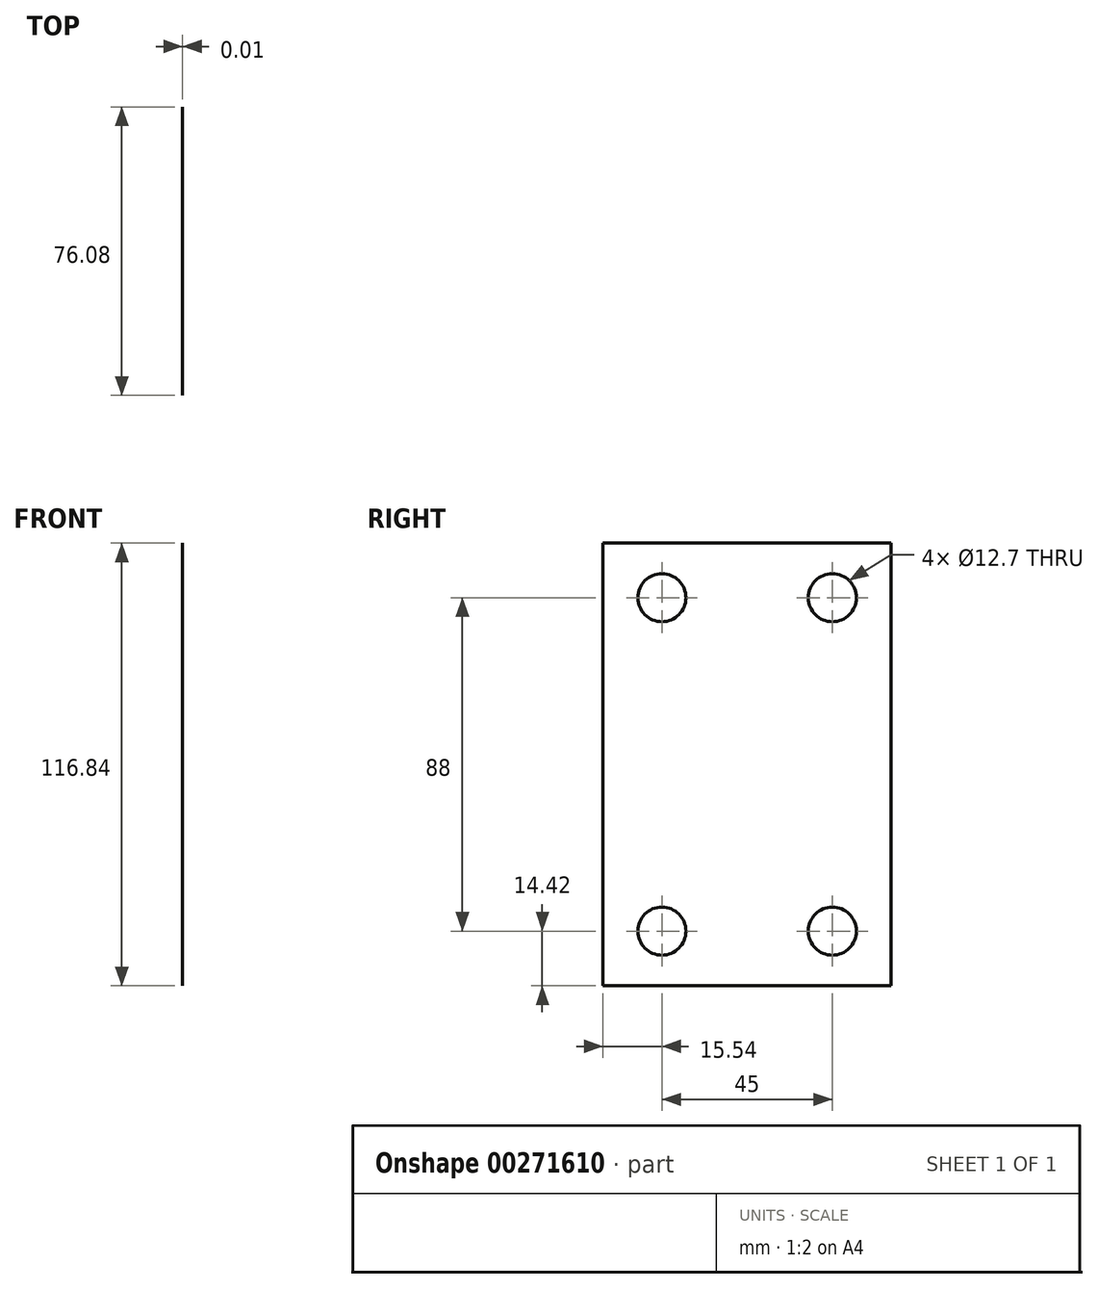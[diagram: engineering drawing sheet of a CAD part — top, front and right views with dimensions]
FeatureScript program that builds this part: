
annotation { "Feature Type Name" : "Feature", "Feature Type Description" : "" }
export const myFeature = defineFeature(function(context is Context, id is Id, definition is map)
    precondition{}
    {
        {
            var Q0;
            Q0=qCreatedBy(makeId("Right.planeOp"),FACE);
            var sketch = newSketch(context, id + "F0", { "sketchPlane" : qUnion([Q0])});
            skLineSegment(sketch, "E0.bottom", {"start": v(38.04, 58.42) * mm, "end": v(-38.04, 58.42) * mm});
            skLineSegment(sketch, "E0.top", {"start": v(38.04, -58.42) * mm, "end": v(-38.04, -58.42) * mm});
            skLineSegment(sketch, "E0.left", {"start": v(38.04, 58.42) * mm, "end": v(38.04, -58.42) * mm});
            skLineSegment(sketch, "E0.right", {"start": v(-38.04, 58.42) * mm, "end": v(-38.04, -58.42) * mm});
            skPoint(sketch, "E0.middle", {"position": v(0, 0) * mm});
            skCircle(sketch, "E1", {"center": v(-22.5, 44) * mm, "radius": 6.35 * mm});
            skCircle(sketch, "E2", {"center": v(-22.5, -44) * mm, "radius": 6.35 * mm});
            skCircle(sketch, "E3", {"center": v(22.5, -44) * mm, "radius": 6.35 * mm});
            skCircle(sketch, "E4", {"center": v(22.5, 44) * mm, "radius": 6.35 * mm});
            skSolve(sketch);
        }
        {
            var Q0;
            Q0=makeQuery(id+"F0.imprint","IMPRINT",FACE,{"disambiguationData":[TD([[makeQuery(id+"F0.imprint","IMPRINT",EDGE,{"derivedFrom":sQuery(id+"F0.wireOp",EDGE,"E0.bottom")}),1.0]])]});
            extrude(context, id + "F1", {"entities" : qUnion([Q0]), "depth" : 3 / 406.4 * mm});
        }
    });
